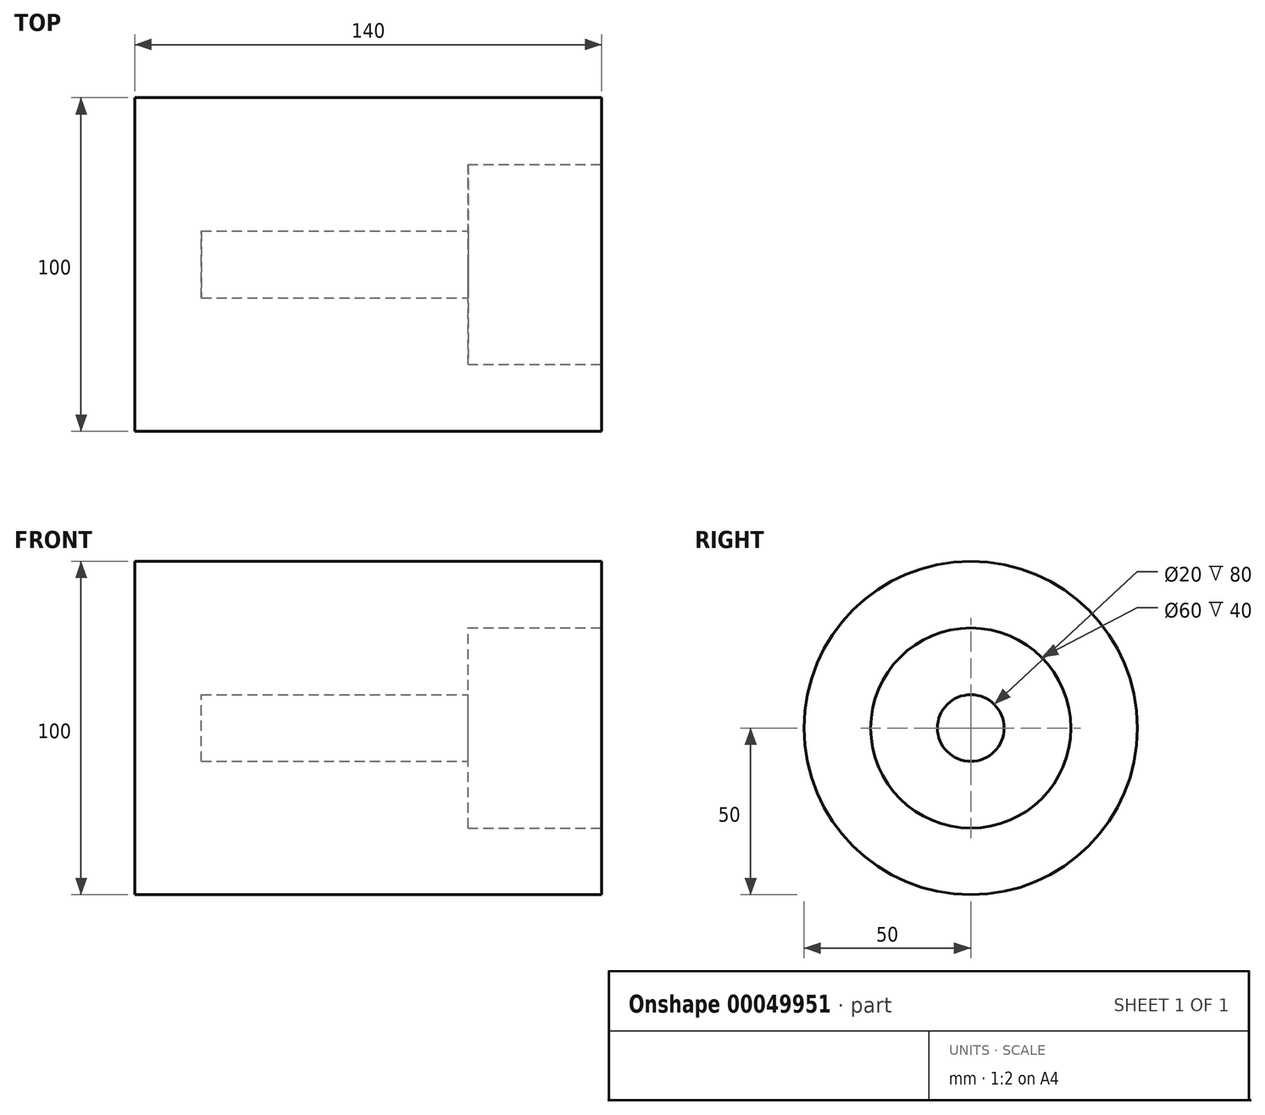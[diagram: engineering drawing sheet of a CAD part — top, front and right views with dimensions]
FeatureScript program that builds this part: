
annotation { "Feature Type Name" : "Feature", "Feature Type Description" : "" }
export const myFeature = defineFeature(function(context is Context, id is Id, definition is map)
    precondition{}
    {
        {
            var Q0;
            Q0=qCreatedBy(makeId("Front.planeOp"),FACE);
            var sketch = newSketch(context, id + "F0", { "sketchPlane" : qUnion([Q0])});
            skLineSegment(sketch, "E0", {"start": v(0, 0) * mm, "end": v(0, 50) * mm});
            skLineSegment(sketch, "E1", {"start": v(0, 50) * mm, "end": v(140, 50) * mm});
            skLineSegment(sketch, "E2", {"start": v(140, 50) * mm, "end": v(140, 0) * mm});
            skLineSegment(sketch, "E3", {"start": v(140, 0) * mm, "end": v(0, 0) * mm});
            skLineSegment(sketch, "E4", {"start": v(20, 0) * mm, "end": v(20, 10) * mm});
            skLineSegment(sketch, "E5", {"start": v(20, 10) * mm, "end": v(100, 10) * mm});
            skLineSegment(sketch, "E6", {"start": v(100, 10) * mm, "end": v(100, 30) * mm});
            skLineSegment(sketch, "E7", {"start": v(100, 10) * mm, "end": v(100, 0) * mm});
            skLineSegment(sketch, "E8", {"start": v(100, 30) * mm, "end": v(140, 30) * mm});
            skSolve(sketch);
        }
        {
            var Q0;
            {var subQ2=sQuery(id+"F0.wireOp",EDGE,"E0");Q0=makeQuery(id+"F0.imprint","IMPRINT",FACE,{"disambiguationData":[TD([[makeQuery(id+"F0.imprint","IMPRINT",EDGE,{"derivedFrom":subQ2}),-1.0]])]});}
            var Q1;
            Q1=sQuery(id+"F0.wireOp",EDGE,"E3");
            revolve(context, id + "F1", {"entities" : qUnion([Q0]), "axis" : qUnion([Q1]), "revolveType" : RevolveType.FULL});
        }
    });
